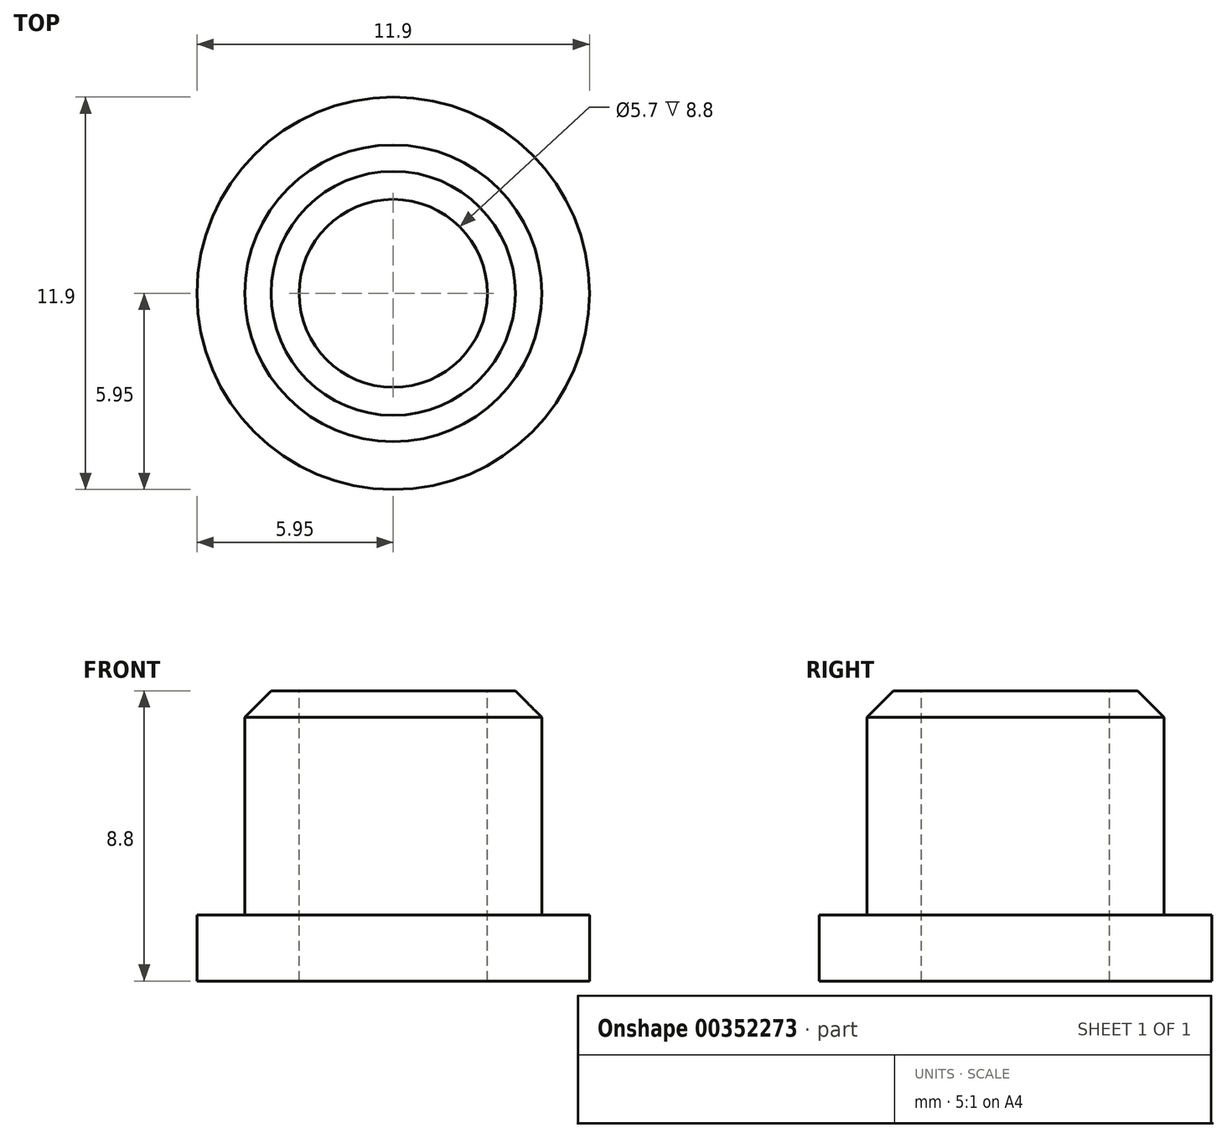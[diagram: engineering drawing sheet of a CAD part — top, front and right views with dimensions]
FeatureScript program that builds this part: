
annotation { "Feature Type Name" : "Feature", "Feature Type Description" : "" }
export const myFeature = defineFeature(function(context is Context, id is Id, definition is map)
    precondition{}
    {
        {
            var Q0;
            Q0=qCreatedBy(makeId("Top.planeOp"),FACE);
            var sketch = newSketch(context, id + "F0", { "sketchPlane" : qUnion([Q0])});
            skCircle(sketch, "E0", {"center": v(0, 0) * mm, "radius": 5.95 * mm});
            skSolve(sketch);
        }
        {
            var Q0;
            Q0 = qSketchRegion(id + "F0", true);
            extrude(context, id + "F1", {"entities" : qUnion([Q0]), "depth" : 2 * mm});
        }
        {
            var Q0;
            Q0=makeQuery(id+"F1.opExtrude","CAP_FACE",FACE,{"disambiguationData":[OSD([sQuery(id+"F0.wireOp",EDGE,"E0")])],"isStart":false});
            var sketch = newSketch(context, id + "F2", { "sketchPlane" : qUnion([Q0])});
            skCircle(sketch, "E1", {"center": v(0, 0) * mm, "radius": 4.5 * mm});
            skSolve(sketch);
        }
        {
            var Q0;
            Q0 = qSketchRegion(id + "F2", true);
            extrude(context, id + "F3", {"entities" : qUnion([Q0]), "operationType" : NewBodyOperationType.ADD, "depth" : 6.8 * mm});
        }
        {
            var Q0;
            Q0=makeQuery(id+"F3.opExtrude","CAP_FACE",FACE,{"disambiguationData":[OSD([sQuery(id+"F2.wireOp",EDGE,"E1")])],"isStart":false});
            var sketch = newSketch(context, id + "F4", { "sketchPlane" : qUnion([Q0])});
            skCircle(sketch, "E2", {"center": v(0, 0) * mm, "radius": 2.85 * mm});
            skSolve(sketch);
        }
        {
            var Q0;
            Q0 = qSketchRegion(id + "F4", true);
            extrude(context, id + "F5", {"entities" : qUnion([Q0]), "operationType" : NewBodyOperationType.REMOVE, "endBound" : BoundingType.THROUGH_ALL, "oppositeDirection" : true, "depth" : 8.7 * mm});
        }
        {
            var Q0;
            Q0=makeQuery(id+"F3.opExtrude","CAP_EDGE",EDGE,{"disambiguationData":[OSD([sQuery(id+"F2.wireOp",EDGE,"E1")])],"isStart":false});
            chamfer(context, id + "F6", {"entities" : qUnion([Q0]), "width" : .8 * mm, "tangentPropagation" : true});
        }
    });
